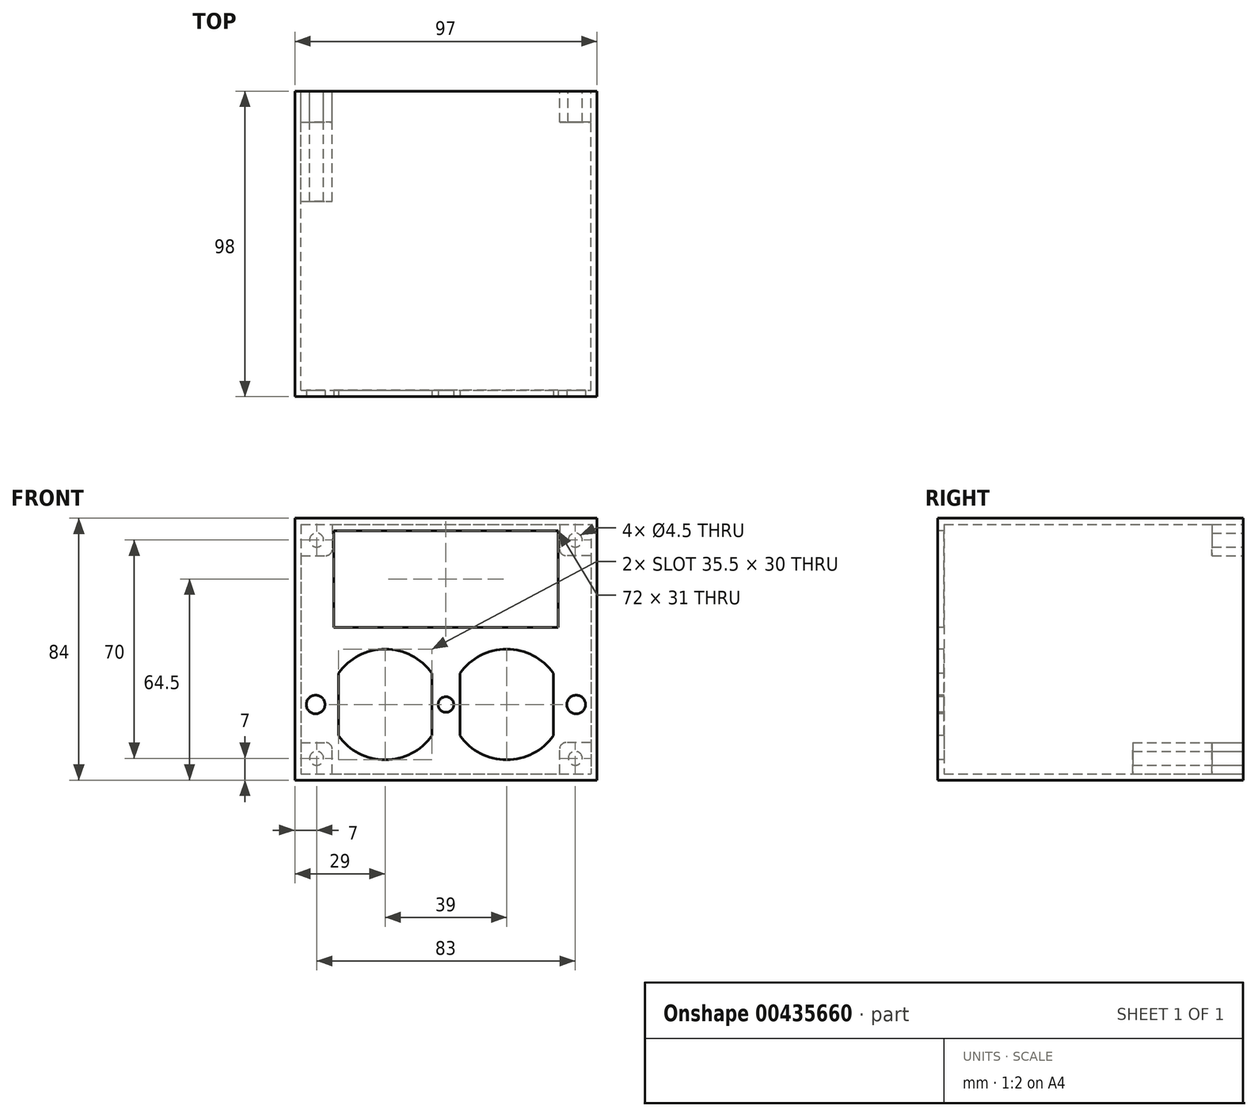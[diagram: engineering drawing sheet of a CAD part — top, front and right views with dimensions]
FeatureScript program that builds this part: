
annotation { "Feature Type Name" : "Feature", "Feature Type Description" : "" }
export const myFeature = defineFeature(function(context is Context, id is Id, definition is map)
    precondition{}
    {
        {
            var Q0;
            Q0=qCreatedBy(makeId("Front.planeOp"),FACE);
            var sketch = newSketch(context, id + "F0", { "sketchPlane" : qUnion([Q0])});
            skLineSegment(sketch, "E0.bottom", {"start": v(-48.5, 42) * mm, "end": v(48.5, 42) * mm});
            skLineSegment(sketch, "E0.top", {"start": v(-48.5, -42) * mm, "end": v(48.5, -42) * mm});
            skLineSegment(sketch, "E0.left", {"start": v(-48.5, 42) * mm, "end": v(-48.5, -42) * mm});
            skLineSegment(sketch, "E0.right", {"start": v(48.5, 42) * mm, "end": v(48.5, -42) * mm});
            skLineSegment(sketch, "E1", {"start": v(-48.5, 42) * mm, "end": v(48.5, -42) * mm, "construction": true});
            skSolve(sketch);
        }
        {
            var Q0;
            Q0=makeQuery(id+"F0.imprint","IMPRINT",FACE,{"disambiguationData":[TD([[makeQuery(id+"F0.imprint","IMPRINT",EDGE,{"derivedFrom":sQuery(id+"F0.wireOp",EDGE,"E0.bottom")}),-1.0]])]});
            extrude(context, id + "F1", {"entities" : qUnion([Q0]), "depth" : 86 * mm + 2 * mm + 10 * mm});
        }
        {
            var Q0;
            Q0=makeQuery(id+"F1.opExtrude","CAP_FACE",FACE,{"disambiguationData":[OSD([sQuery(id+"F0.wireOp",EDGE,"E0.bottom"),sQuery(id+"F0.wireOp",EDGE,"E0.top"),sQuery(id+"F0.wireOp",EDGE,"E0.left"),sQuery(id+"F0.wireOp",EDGE,"E0.right")])],"isStart":true});
            shell(context, id + "F2", {"entities" : qUnion([Q0]), "thickness" : 2 * mm});
        }
        {
            var Q0;
            Q0=makeQuery(id+"F1.opExtrude","CAP_FACE",FACE,{"disambiguationData":[OSD([sQuery(id+"F0.wireOp",EDGE,"E0.bottom"),sQuery(id+"F0.wireOp",EDGE,"E0.top"),sQuery(id+"F0.wireOp",EDGE,"E0.left"),sQuery(id+"F0.wireOp",EDGE,"E0.right")])],"isStart":false});
            var sketch = newSketch(context, id + "F3", { "sketchPlane" : qUnion([Q0])});
            skLineSegment(sketch, "E2", {"start": v(-34.5, -7.75) * mm, "end": v(-34.5, -27.75) * mm});
            skLineSegment(sketch, "E3", {"start": v(-4.5, -7.75) * mm, "end": v(-4.5, -27.75) * mm});
            skArc(sketch, "E4", {"start": v(-4.5, -7.75) * mm, "mid": v(-19.5, 0) * mm, "end": v(-34.5, -7.75) * mm});
            skArc(sketch, "E5", {"start": v(-34.5, -27.75) * mm, "mid": v(-19.5, -35.5) * mm, "end": v(-4.5, -27.75) * mm});
            skLineSegment(sketch, "E6.bottom", {"start": v(-34.5, 0) * mm, "end": v(-4.5, 0) * mm, "construction": true});
            skLineSegment(sketch, "E6.top", {"start": v(-34.5, -35.5) * mm, "end": v(-4.5, -35.5) * mm, "construction": true});
            skLineSegment(sketch, "E6.left", {"start": v(-34.5, 0) * mm, "end": v(-34.5, -35.5) * mm, "construction": true});
            skLineSegment(sketch, "E6.right", {"start": v(-4.5, 0) * mm, "end": v(-4.5, -35.5) * mm, "construction": true});
            skLineSegment(sketch, "E7", {"start": v(0, 42) * mm, "end": v(0, -42) * mm, "construction": true});
            skLineSegment(sketch, "E8.bottom", {"start": v(-36, 38) * mm, "end": v(36, 38) * mm});
            skLineSegment(sketch, "E8.top", {"start": v(-36, 7) * mm, "end": v(36, 7) * mm});
            skLineSegment(sketch, "E8.left", {"start": v(-36, 38) * mm, "end": v(-36, 7) * mm});
            skLineSegment(sketch, "E8.right", {"start": v(36, 38) * mm, "end": v(36, 7) * mm});
            skLineSegment(sketch, "E9", {"start": v(-36, 22.5) * mm, "end": v(0, 22.5) * mm, "construction": true});
            skLineSegment(sketch, "E10", {"start": v(0, 22.5) * mm, "end": v(36, 22.5) * mm, "construction": true});
            skLineSegment(sketch, "E11.MirrorCS", {"start": v(34.5, -7.75) * mm, "end": v(34.5, -27.75) * mm});
            skLineSegment(sketch, "E12.MirrorCS", {"start": v(4.5, -7.75) * mm, "end": v(4.5, -27.75) * mm});
            skArc(sketch, "E13.MirrorCS", {"start": v(4.5, -7.75) * mm, "mid": v(19.5, 0) * mm, "end": v(34.5, -7.75) * mm});
            skLineSegment(sketch, "E14.MirrorCS", {"start": v(4.5, 0) * mm, "end": v(4.5, -35.5) * mm, "construction": true});
            skLineSegment(sketch, "E15.MirrorCS", {"start": v(34.5, 0) * mm, "end": v(34.5, -35.5) * mm, "construction": true});
            skLineSegment(sketch, "E16.MirrorCS", {"start": v(34.5, -35.5) * mm, "end": v(4.5, -35.5) * mm, "construction": true});
            skLineSegment(sketch, "E17.MirrorCS", {"start": v(34.5, 0) * mm, "end": v(4.5, 0) * mm, "construction": true});
            skArc(sketch, "E18.MirrorCS", {"start": v(34.5, -27.75) * mm, "mid": v(19.5, -35.5) * mm, "end": v(4.5, -27.75) * mm});
            skCircle(sketch, "E19", {"center": v(0, -17.75) * mm, "radius": 2.5 * mm});
            skLineSegment(sketch, "E20", {"start": v(-4.5, -17.75) * mm, "end": v(0, -17.75) * mm, "construction": true});
            skCircle(sketch, "E21", {"center": v(-41.8, -17.75) * mm, "radius": 3 * mm});
            skPoint(sketch, "E21.centerSnap0", {"position": v(-34.5, -17.75) * mm});
            skCircle(sketch, "E22", {"center": v(41.8, -17.75) * mm, "radius": 3 * mm});
            skLineSegment(sketch, "E23", {"start": v(-34.5, -17.75) * mm, "end": v(-41.8, -17.75) * mm, "construction": true});
            skLineSegment(sketch, "E24", {"start": v(41.8, -17.75) * mm, "end": v(34.5, -17.75) * mm, "construction": true});
            skSolve(sketch);
        }
        {
            var Q0;
            Q0=qSketchRegion(id+"F3",true);
            extrude(context, id + "F4", {"entities" : qUnion([Q0]), "operationType" : NewBodyOperationType.REMOVE, "endBound" : BoundingType.UP_TO_NEXT, "oppositeDirection" : true, "depth" : 25.4 * mm});
        }
        {
            var Q0;
            Q0=makeQuery(id+"F1.opExtrude","CAP_FACE",FACE,{"disambiguationData":[OSD([sQuery(id+"F0.wireOp",EDGE,"E0.bottom"),sQuery(id+"F0.wireOp",EDGE,"E0.top"),sQuery(id+"F0.wireOp",EDGE,"E0.left"),sQuery(id+"F0.wireOp",EDGE,"E0.right")])],"isStart":true});
            var sketch = newSketch(context, id + "F5", { "sketchPlane" : qUnion([Q0])});
            skLineSegment(sketch, "E25.bottom", {"start": v(-46.5, 40) * mm, "end": v(-36.5, 40) * mm});
            skLineSegment(sketch, "E25.top", {"start": v(-46.5, 30) * mm, "end": v(-36.5, 30) * mm});
            skLineSegment(sketch, "E25.left", {"start": v(-46.5, 40) * mm, "end": v(-46.5, 30) * mm});
            skLineSegment(sketch, "E25.right", {"start": v(-36.5, 40) * mm, "end": v(-36.5, 30) * mm});
            skLineSegment(sketch, "E26.bottom", {"start": v(46.5, 40) * mm, "end": v(36.5, 40) * mm});
            skLineSegment(sketch, "E26.top", {"start": v(46.5, 30) * mm, "end": v(36.5, 30) * mm});
            skLineSegment(sketch, "E26.left", {"start": v(46.5, 40) * mm, "end": v(46.5, 30) * mm});
            skLineSegment(sketch, "E26.right", {"start": v(36.5, 40) * mm, "end": v(36.5, 30) * mm});
            skLineSegment(sketch, "E27.bottom", {"start": v(-46.5, -40) * mm, "end": v(-36.5, -40) * mm});
            skLineSegment(sketch, "E27.top", {"start": v(-46.5, -30) * mm, "end": v(-36.5, -30) * mm});
            skLineSegment(sketch, "E27.left", {"start": v(-46.5, -40) * mm, "end": v(-46.5, -30) * mm});
            skLineSegment(sketch, "E27.right", {"start": v(-36.5, -40) * mm, "end": v(-36.5, -30) * mm});
            skLineSegment(sketch, "E28.bottom", {"start": v(46.5, -40) * mm, "end": v(36.5, -40) * mm});
            skLineSegment(sketch, "E28.top", {"start": v(46.5, -30) * mm, "end": v(36.5, -30) * mm});
            skLineSegment(sketch, "E28.left", {"start": v(46.5, -40) * mm, "end": v(46.5, -30) * mm});
            skLineSegment(sketch, "E28.right", {"start": v(36.5, -40) * mm, "end": v(36.5, -30) * mm});
            skCircle(sketch, "E29", {"center": v(-41.5, 35) * mm, "radius": 2.25 * mm});
            skCircle(sketch, "E30", {"center": v(-41.5, -35) * mm, "radius": 2.25 * mm});
            skCircle(sketch, "E31", {"center": v(41.5, 35) * mm, "radius": 2.25 * mm});
            skCircle(sketch, "E32", {"center": v(41.5, -35) * mm, "radius": 2.25 * mm});
            skLineSegment(sketch, "E33", {"start": v(-46.5, 40) * mm, "end": v(-36.5, 30) * mm, "construction": true});
            skLineSegment(sketch, "E34", {"start": v(36.5, -30) * mm, "end": v(46.5, -40) * mm, "construction": true});
            skSolve(sketch);
        }
        {
            var Q0;
            Q0=qSketchRegion(id+"F5",true);
            extrude(context, id + "F6", {"entities" : qUnion([Q0]), "operationType" : NewBodyOperationType.ADD, "oppositeDirection" : true, "depth" : 10 * mm});
        }
        {
            var Q0;
            Q0=makeQuery(id+"F6.opExtrude","SWEPT_EDGE",EDGE,{"disambiguationData":[OSD([sQuery(id+"F0.wireOp",EDGE,"E0.bottom"),sQuery(id+"F5.wireOp",EDGE,"E25.bottom"),sQuery(id+"F5.wireOp",EDGE,"E25.right")])]});
            var Q1;
            Q1=makeQuery(id+"F6.opExtrude","SWEPT_EDGE",EDGE,{"disambiguationData":[OSD([sQuery(id+"F0.wireOp",EDGE,"E0.right"),sQuery(id+"F5.wireOp",EDGE,"E25.top"),sQuery(id+"F5.wireOp",EDGE,"E25.left")])]});
            var Q2;
            Q2=makeQuery(id+"F6.opExtrude","SWEPT_EDGE",EDGE,{"disambiguationData":[OSD([sQuery(id+"F0.wireOp",EDGE,"E0.bottom"),sQuery(id+"F5.wireOp",EDGE,"E26.bottom"),sQuery(id+"F5.wireOp",EDGE,"E26.right")])]});
            var Q3;
            Q3=makeQuery(id+"F6.opExtrude","SWEPT_EDGE",EDGE,{"disambiguationData":[OSD([sQuery(id+"F0.wireOp",EDGE,"E0.left"),sQuery(id+"F5.wireOp",EDGE,"E26.top"),sQuery(id+"F5.wireOp",EDGE,"E26.left")])]});
            var Q4;
            Q4=makeQuery(id+"F6.opExtrude","SWEPT_EDGE",EDGE,{"disambiguationData":[OSD([sQuery(id+"F0.wireOp",EDGE,"E0.top"),sQuery(id+"F5.wireOp",EDGE,"E28.bottom"),sQuery(id+"F5.wireOp",EDGE,"E28.right")])]});
            var Q5;
            Q5=makeQuery(id+"F6.opExtrude","SWEPT_EDGE",EDGE,{"disambiguationData":[OSD([sQuery(id+"F0.wireOp",EDGE,"E0.left"),sQuery(id+"F5.wireOp",EDGE,"E28.top"),sQuery(id+"F5.wireOp",EDGE,"E28.left")])]});
            var Q6;
            Q6=makeQuery(id+"F6.opExtrude","SWEPT_EDGE",EDGE,{"disambiguationData":[OSD([sQuery(id+"F0.wireOp",EDGE,"E0.top"),sQuery(id+"F5.wireOp",EDGE,"E27.bottom"),sQuery(id+"F5.wireOp",EDGE,"E27.right")])]});
            var Q7;
            Q7=makeQuery(id+"F6.opExtrude","SWEPT_EDGE",EDGE,{"disambiguationData":[OSD([sQuery(id+"F0.wireOp",EDGE,"E0.right"),sQuery(id+"F5.wireOp",EDGE,"E27.top"),sQuery(id+"F5.wireOp",EDGE,"E27.left")])]});
            var Q8;
            Q8=makeQuery(id+"F6.opExtrude","SWEPT_EDGE",EDGE,{"disambiguationData":[OSD([sQuery(id+"F5.wireOp",EDGE,"E25.top"),sQuery(id+"F5.wireOp",EDGE,"E25.right")])]});
            var Q9;
            Q9=makeQuery(id+"F6.opExtrude","SWEPT_EDGE",EDGE,{"disambiguationData":[OSD([sQuery(id+"F5.wireOp",EDGE,"E27.top"),sQuery(id+"F5.wireOp",EDGE,"E27.right")])]});
            var Q10;
            Q10=makeQuery(id+"F6.opExtrude","SWEPT_EDGE",EDGE,{"disambiguationData":[OSD([sQuery(id+"F5.wireOp",EDGE,"E26.top"),sQuery(id+"F5.wireOp",EDGE,"E26.right")])]});
            var Q11;
            Q11=makeQuery(id+"F6.opExtrude","SWEPT_EDGE",EDGE,{"disambiguationData":[OSD([sQuery(id+"F5.wireOp",EDGE,"E28.top"),sQuery(id+"F5.wireOp",EDGE,"E28.right")])]});
            fillet(context, id + "F7", {"entities" : qUnion([Q0, Q1, Q2, Q3, Q4, Q5, Q6, Q7, Q8, Q9, Q10, Q11]), "radius" : 2 * mm, "tangentPropagation" : true, "allowEdgeOverflow" : false});
        }
        {
            var Q0;
            Q0=makeQuery(id+"F6.opExtrude","CAP_FACE",FACE,{"disambiguationData":[OSD([sQuery(id+"F5.wireOp",EDGE,"E28.bottom"),sQuery(id+"F5.wireOp",EDGE,"E28.top"),sQuery(id+"F5.wireOp",EDGE,"E28.left"),sQuery(id+"F5.wireOp",EDGE,"E28.right"),sQuery(id+"F5.wireOp",EDGE,"E32")])],"isStart":false});
            extrude(context, id + "F8", {"entities" : qUnion([Q0]), "operationType" : NewBodyOperationType.ADD, "depth" : 25.4 * mm});
        }
    });
